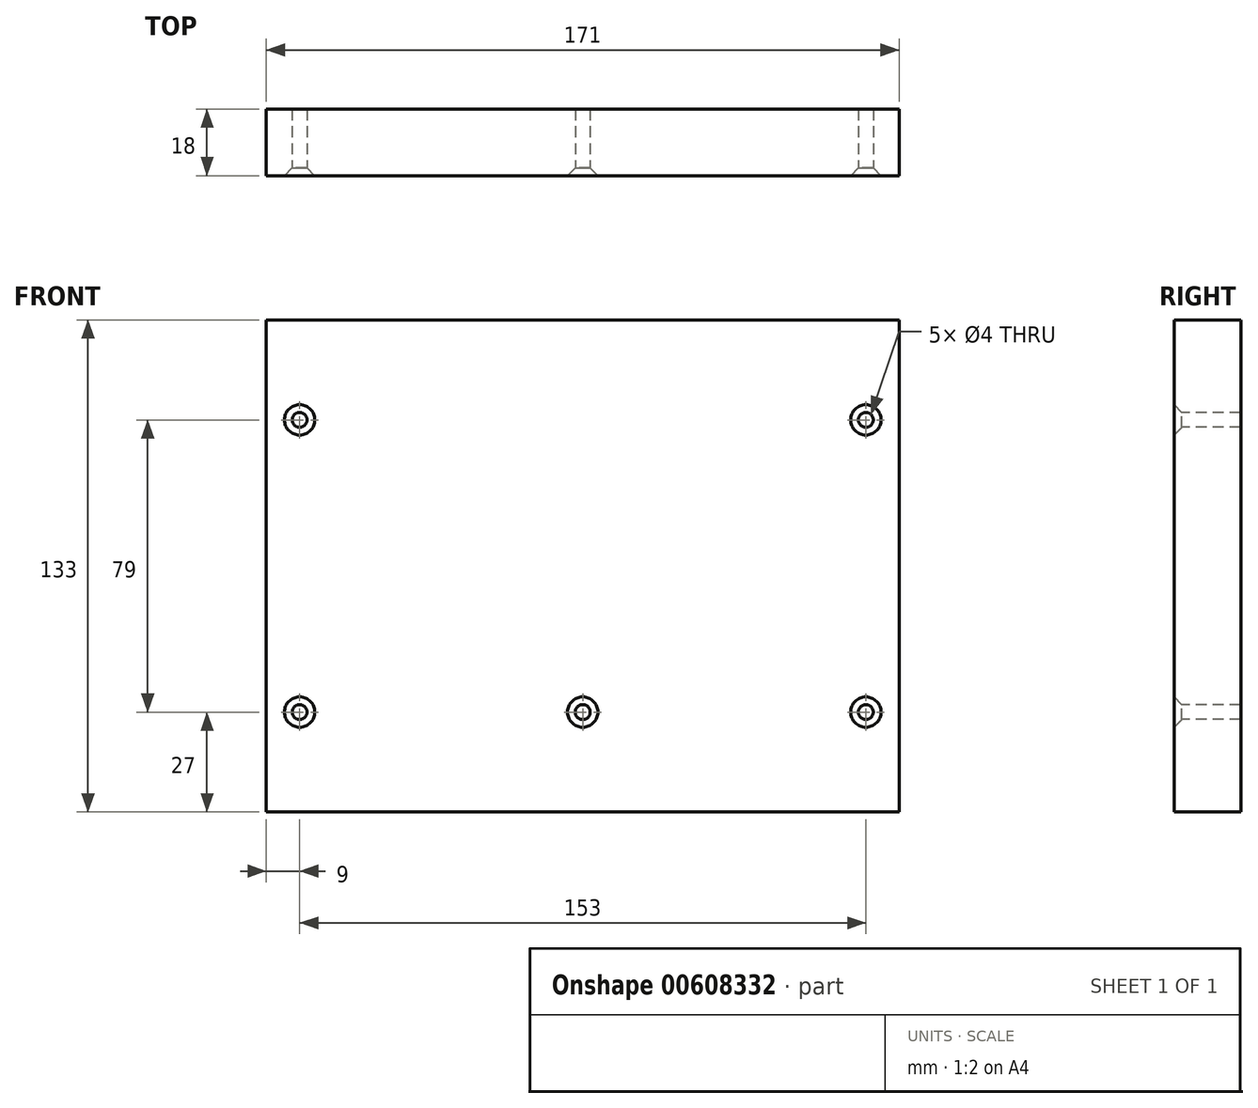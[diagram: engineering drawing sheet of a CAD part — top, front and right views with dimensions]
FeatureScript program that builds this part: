
annotation { "Feature Type Name" : "Feature", "Feature Type Description" : "" }
export const myFeature = defineFeature(function(context is Context, id is Id, definition is map)
    precondition{}
    {
        {
            var Q0;
            Q0=qCreatedBy(makeId("Front.planeOp"),FACE);
            var sketch = newSketch(context, id + "F0", { "sketchPlane" : qUnion([Q0])});
            skLineSegment(sketch, "E0.bottom", {"start": v(85.5, -66.5) * mm, "end": v(-85.5, -66.5) * mm});
            skLineSegment(sketch, "E0.top", {"start": v(85.5, 66.5) * mm, "end": v(-85.5, 66.5) * mm});
            skLineSegment(sketch, "E0.left", {"start": v(85.5, -66.5) * mm, "end": v(85.5, 66.5) * mm});
            skLineSegment(sketch, "E0.right", {"start": v(-85.5, -66.5) * mm, "end": v(-85.5, 66.5) * mm});
            skPoint(sketch, "E0.middle", {"position": v(0, 0) * mm});
            skPoint(sketch, "E1", {"position": v(0, 103.5) * mm});
            skSolve(sketch);
        }
        {
            var Q0;
            Q0=makeQuery(id+"F0.imprint","IMPRINT",FACE,{"disambiguationData":[TD([[makeQuery(id+"F0.imprint","IMPRINT",EDGE,{"derivedFrom":sQuery(id+"F0.wireOp",EDGE,"E0.bottom")}),-1.0]])]});
            extrude(context, id + "F1", {"entities" : qUnion([Q0]), "depth" : 18 * mm, "offsetDistance" : 25 * mm});
        }
        {
            var Q0;
            Q0=sQuery(id+"F0.wireOp",VERTEX,"E1");
            var Q1;
            Q1=makeQuery(id+"F1.opExtrude","SWEPT_BODY",BODY,{"disambiguationData":[OSD([sQuery(id+"F0.wireOp",EDGE,"E0.bottom"),sQuery(id+"F0.wireOp",EDGE,"E0.top"),sQuery(id+"F0.wireOp",EDGE,"E0.left"),sQuery(id+"F0.wireOp",EDGE,"E0.right")])]});
            hole(context, id + "F2", {"style" : HoleStyle.SIMPLE, "endStyle" : HoleEndStyle.THROUGH, "oppositeDirection" : true, "holeDiameter" : 32 * mm, "majorDiameter" : 5 * mm, "isTappedThrough" : true, "tappedDepth" : 12 * mm, "tapClearance" : 3, "locations" : qUnion([Q0]), "scope" : qUnion([Q1])});
        }
        {
            var Q0;
            Q0=makeQuery(id+"F1.opExtrude","CAP_FACE",FACE,{"disambiguationData":[OSD([sQuery(id+"F0.wireOp",EDGE,"E0.bottom"),sQuery(id+"F0.wireOp",EDGE,"E0.top"),sQuery(id+"F0.wireOp",EDGE,"E0.left"),sQuery(id+"F0.wireOp",EDGE,"E0.right")])],"isStart":false});
            var sketch = newSketch(context, id + "F3", { "sketchPlane" : qUnion([Q0])});
            skPoint(sketch, "E2", {"position": v(0, -39.5) * mm});
            skPoint(sketch, "E3", {"position": v(-76.5, -39.5) * mm});
            skPoint(sketch, "E4", {"position": v(76.5, -39.5) * mm});
            skPoint(sketch, "E5", {"position": v(76.5, 118.5) * mm});
            skPoint(sketch, "E6", {"position": v(-76.5, 118.5) * mm});
            skPoint(sketch, "E7", {"position": v(-76.5, 39.5) * mm});
            skPoint(sketch, "E8", {"position": v(76.5, 39.5) * mm});
            skSolve(sketch);
        }
        {
            var Q0;
            Q0=sQuery(id+"F3.wireOp",VERTEX,"E2");
            var Q1;
            Q1=makeQuery(id+"F1.opExtrude","SWEPT_BODY",BODY,{"disambiguationData":[OSD([sQuery(id+"F0.wireOp",EDGE,"E0.bottom"),sQuery(id+"F0.wireOp",EDGE,"E0.top"),sQuery(id+"F0.wireOp",EDGE,"E0.left"),sQuery(id+"F0.wireOp",EDGE,"E0.right")])]});
            hole(context, id + "F4", {"style" : HoleStyle.C_SINK, "endStyle" : HoleEndStyle.THROUGH, "holeDiameter" : 4 * mm, "cSinkDiameter" : 8.2 * mm, "cSinkAngle" : 90 * degree, "majorDiameter" : 5 * mm, "isTappedThrough" : true, "tappedDepth" : 12 * mm, "tapClearance" : 3, "locations" : qUnion([Q0]), "scope" : qUnion([Q1])});
        }
        {
            var Q0;
            Q0=sQuery(id+"F3.wireOp",VERTEX,"E3");
            var Q1;
            Q1=sQuery(id+"F3.wireOp",VERTEX,"E4");
            var Q2;
            Q2=makeQuery(id+"F1.opExtrude","SWEPT_BODY",BODY,{"disambiguationData":[OSD([sQuery(id+"F0.wireOp",EDGE,"E0.bottom"),sQuery(id+"F0.wireOp",EDGE,"E0.top"),sQuery(id+"F0.wireOp",EDGE,"E0.left"),sQuery(id+"F0.wireOp",EDGE,"E0.right")])]});
            hole(context, id + "F5", {"style" : HoleStyle.C_SINK, "endStyle" : HoleEndStyle.THROUGH, "holeDiameter" : 4 * mm, "cSinkDiameter" : 8.2 * mm, "cSinkAngle" : 90 * degree, "majorDiameter" : 5 * mm, "isTappedThrough" : true, "tappedDepth" : 12 * mm, "tapClearance" : 3, "locations" : qUnion([Q0, Q1]), "scope" : qUnion([Q2])});
        }
        {
            var Q0;
            Q0=sQuery(id+"F3.wireOp",VERTEX,"E6");
            var Q1;
            Q1=sQuery(id+"F3.wireOp",VERTEX,"E5");
            var Q2;
            Q2=makeQuery(id+"F1.opExtrude","SWEPT_BODY",BODY,{"disambiguationData":[OSD([sQuery(id+"F0.wireOp",EDGE,"E0.bottom"),sQuery(id+"F0.wireOp",EDGE,"E0.top"),sQuery(id+"F0.wireOp",EDGE,"E0.left"),sQuery(id+"F0.wireOp",EDGE,"E0.right")])]});
            hole(context, id + "F6", {"style" : HoleStyle.C_SINK, "endStyle" : HoleEndStyle.THROUGH, "holeDiameter" : 4 * mm, "cSinkDiameter" : 8.2 * mm, "cSinkAngle" : 90 * degree, "majorDiameter" : 5 * mm, "isTappedThrough" : true, "tappedDepth" : 12 * mm, "tapClearance" : 3, "locations" : qUnion([Q0, Q1]), "scope" : qUnion([Q2])});
        }
        {
            var Q0;
            Q0=sQuery(id+"F3.wireOp",VERTEX,"E7");
            var Q1;
            Q1=sQuery(id+"F3.wireOp",VERTEX,"E8");
            var Q2;
            Q2=makeQuery(id+"F1.opExtrude","SWEPT_BODY",BODY,{"disambiguationData":[OSD([sQuery(id+"F0.wireOp",EDGE,"E0.bottom"),sQuery(id+"F0.wireOp",EDGE,"E0.top"),sQuery(id+"F0.wireOp",EDGE,"E0.left"),sQuery(id+"F0.wireOp",EDGE,"E0.right")])]});
            hole(context, id + "F7", {"style" : HoleStyle.C_SINK, "endStyle" : HoleEndStyle.THROUGH, "holeDiameter" : 4 * mm, "cSinkDiameter" : 8.2 * mm, "cSinkAngle" : 90 * degree, "majorDiameter" : 5 * mm, "isTappedThrough" : true, "tappedDepth" : 12 * mm, "tapClearance" : 3, "locations" : qUnion([Q0, Q1]), "scope" : qUnion([Q2])});
        }
    });
